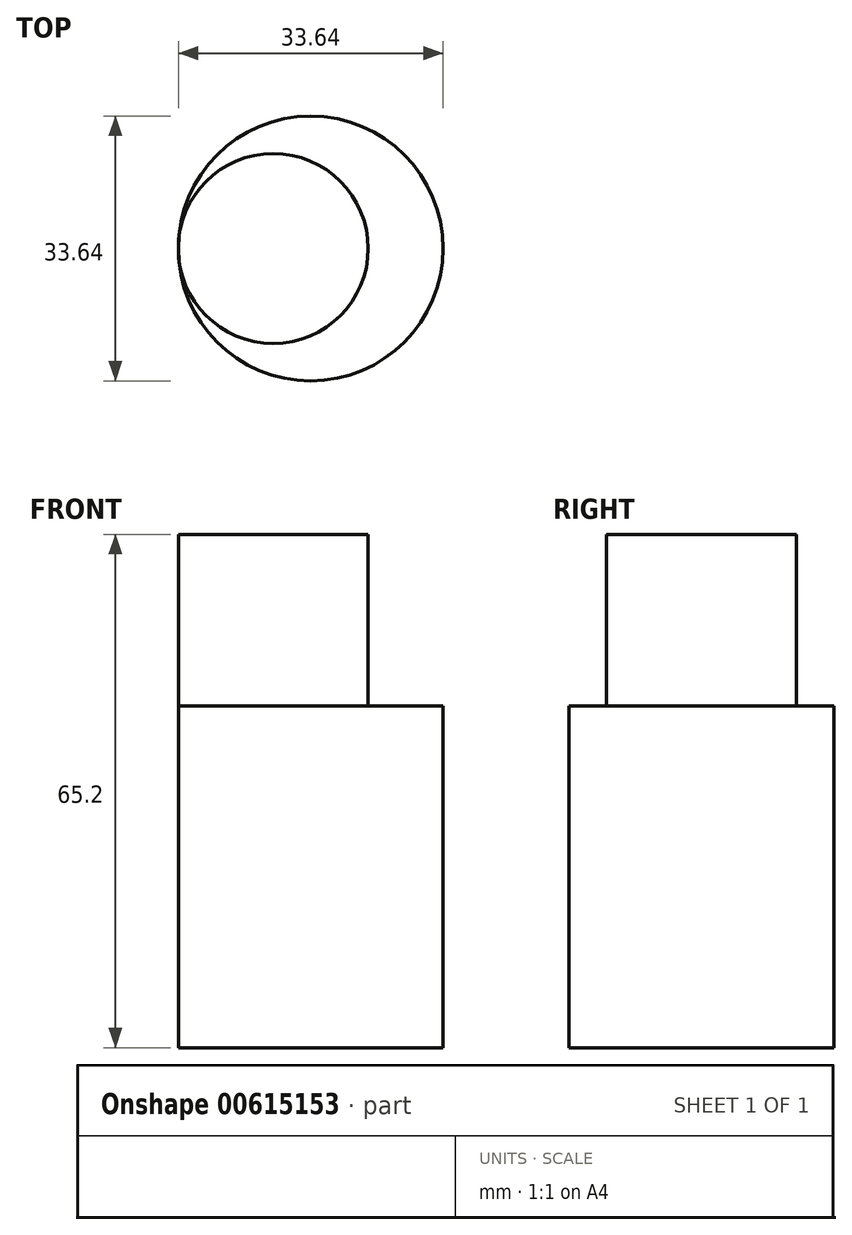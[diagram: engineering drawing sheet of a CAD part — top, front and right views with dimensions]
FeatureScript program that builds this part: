
annotation { "Feature Type Name" : "Feature", "Feature Type Description" : "" }
export const myFeature = defineFeature(function(context is Context, id is Id, definition is map)
    precondition{}
    {
        {
            var Q0;
            Q0=qCreatedBy(makeId("Front.planeOp"),FACE);
            var sketch = newSketch(context, id + "F0", { "sketchPlane" : qUnion([Q0])});
            skLineSegment(sketch, "E0.bottom", {"start": v(0, 0) * mm, "end": v(16.82, 0) * mm});
            skLineSegment(sketch, "E0.top", {"start": v(0, 43.44) * mm, "end": v(16.82, 43.44) * mm});
            skLineSegment(sketch, "E0.left", {"start": v(0, 0) * mm, "end": v(0, 43.44) * mm});
            skLineSegment(sketch, "E0.right", {"start": v(16.82, 0) * mm, "end": v(16.82, 43.44) * mm});
            skSolve(sketch);
        }
        {
            var Q0;
            Q0=makeQuery(id+"F0.imprint","IMPRINT",FACE,{"disambiguationData":[TD([[makeQuery(id+"F0.imprint","IMPRINT",EDGE,{"derivedFrom":sQuery(id+"F0.wireOp",EDGE,"E0.bottom")}),1.0]])]});
            var Q1;
            Q1=sQuery(id+"F0.wireOp",EDGE,"E0.right");
            revolve(context, id + "F1", {"entities" : qUnion([Q0]), "axis" : qUnion([Q1]), "revolveType" : RevolveType.FULL});
        }
        {
            var Q0;
            Q0=qCreatedBy(makeId("Front.planeOp"),FACE);
            var sketch = newSketch(context, id + "F2", { "sketchPlane" : qUnion([Q0])});
            skLineSegment(sketch, "E1.bottom", {"start": v(0, 0) * mm, "end": v(12.06, 0) * mm});
            skLineSegment(sketch, "E1.top", {"start": v(0, 65.2) * mm, "end": v(12.06, 65.2) * mm});
            skLineSegment(sketch, "E1.left", {"start": v(0, 0) * mm, "end": v(0, 65.2) * mm});
            skLineSegment(sketch, "E1.right", {"start": v(12.06, 0) * mm, "end": v(12.06, 65.2) * mm});
            skSolve(sketch);
        }
        {
            var Q0;
            Q0=makeQuery(id+"F2.imprint","IMPRINT",FACE,{"disambiguationData":[TD([[makeQuery(id+"F2.imprint","IMPRINT",EDGE,{"derivedFrom":sQuery(id+"F2.wireOp",EDGE,"E1.bottom")}),1.0]])]});
            var Q1;
            Q1=sQuery(id+"F2.wireOp",EDGE,"E1.right");
            revolve(context, id + "F3", {"operationType" : NewBodyOperationType.ADD, "entities" : qUnion([Q0]), "axis" : qUnion([Q1]), "revolveType" : RevolveType.FULL});
        }
    });
